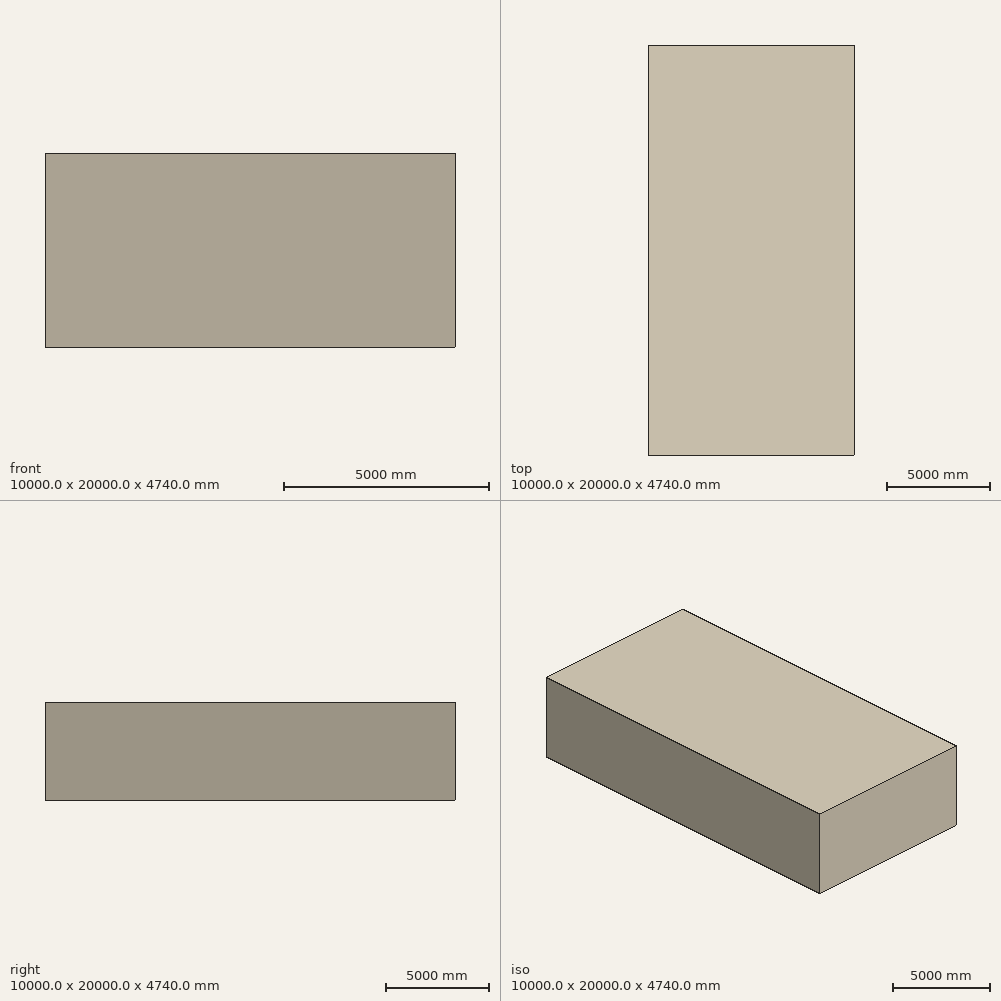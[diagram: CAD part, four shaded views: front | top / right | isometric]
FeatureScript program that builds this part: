
annotation { "Feature Type Name" : "Feature", "Feature Type Description" : "" }
export const myFeature = defineFeature(function(context is Context, id is Id, definition is map)
    precondition{}
    {
        {
            var Q0;
            Q0=qCreatedBy(makeId("Top.planeOp"),FACE);
            var sketch = newSketch(context, id + "F0", { "sketchPlane" : qUnion([Q0])});
            skLineSegment(sketch, "E0.bottom", {"start": v(9890.7, -77.95) * mm, "end": v(-109.3, -77.95) * mm});
            skLineSegment(sketch, "E0.top", {"start": v(9890.7, 19922.05) * mm, "end": v(-109.3, 19922.05) * mm});
            skLineSegment(sketch, "E0.left", {"start": v(9890.7, -77.95) * mm, "end": v(9890.7, 19922.05) * mm});
            skLineSegment(sketch, "E0.right", {"start": v(-109.3, -77.95) * mm, "end": v(-109.3, 19922.05) * mm});
            skSolve(sketch);
        }
        {
            var Q0;
            Q0=makeQuery(id+"F0.imprint","IMPRINT",FACE,{"disambiguationData":[TD([[makeQuery(id+"F0.imprint","IMPRINT",EDGE,{"derivedFrom":sQuery(id+"F0.wireOp",EDGE,"E0.bottom")}),-1.0]])]});
            extrude(context, id + "F1", {"entities" : qUnion([Q0]), "depth" : 4740 * mm});
        }
    });
